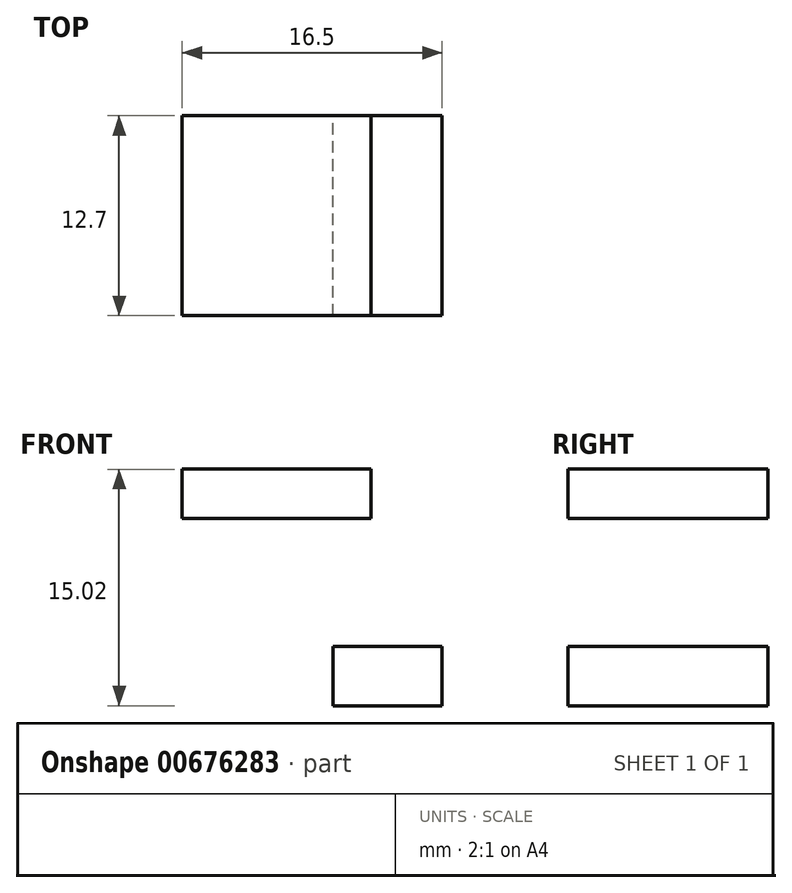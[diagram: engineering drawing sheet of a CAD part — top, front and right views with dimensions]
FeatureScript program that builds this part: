
annotation { "Feature Type Name" : "Feature", "Feature Type Description" : "" }
export const myFeature = defineFeature(function(context is Context, id is Id, definition is map)
    precondition{}
    {
        {
            var Q0;
            Q0=qCreatedBy(makeId("Front.planeOp"),FACE);
            var sketch = newSketch(context, id + "F0", { "sketchPlane" : qUnion([Q0])});
            skLineSegment(sketch, "E0.bottom", {"start": v(0, 0) * mm, "end": v(-6.91, 0) * mm});
            skLineSegment(sketch, "E0.top", {"start": v(0, 3.78) * mm, "end": v(-6.91, 3.78) * mm});
            skLineSegment(sketch, "E0.left", {"start": v(0, 0) * mm, "end": v(0, 3.78) * mm});
            skLineSegment(sketch, "E0.right", {"start": v(-6.91, 0) * mm, "end": v(-6.91, 3.78) * mm});
            skLineSegment(sketch, "E1.bottom", {"start": v(0, 3.78) * mm, "end": v(-4.52, 3.78) * mm});
            skLineSegment(sketch, "E1.top", {"start": v(0, 15.02) * mm, "end": v(-4.52, 15.02) * mm});
            skLineSegment(sketch, "E1.left", {"start": v(0, 3.78) * mm, "end": v(0, 15.02) * mm});
            skLineSegment(sketch, "E1.right", {"start": v(-4.52, 3.78) * mm, "end": v(-4.52, 15.02) * mm});
            skLineSegment(sketch, "E2.bottom", {"start": v(-4.52, 15.02) * mm, "end": v(-16.5, 15.02) * mm});
            skLineSegment(sketch, "E2.top", {"start": v(-4.52, 11.9) * mm, "end": v(-16.5, 11.9) * mm});
            skLineSegment(sketch, "E2.left", {"start": v(-4.52, 15.02) * mm, "end": v(-4.52, 11.9) * mm});
            skLineSegment(sketch, "E2.right", {"start": v(-16.5, 15.02) * mm, "end": v(-16.5, 11.9) * mm});
            skSolve(sketch);
        }
        {
            var Q0;
            Q0=makeQuery(id+"F0.imprint","IMPRINT",FACE,{"disambiguationData":[TD([[makeQuery(id+"F0.imprint","IMPRINT",EDGE,{"derivedFrom":sQuery(id+"F0.wireOp",EDGE,"E1.bottom")}),-1.0]])]});
            var Q1;
            Q1=makeQuery(id+"F0.imprint","IMPRINT",FACE,{"disambiguationData":[TD([[makeQuery(id+"F0.imprint","IMPRINT",EDGE,{"derivedFrom":sQuery(id+"F0.wireOp",EDGE,"E0.bottom")}),-1.0]])]});
            var Q2;
            Q2=makeQuery(id+"F0.imprint","IMPRINT",FACE,{"disambiguationData":[TD([[makeQuery(id+"F0.imprint","IMPRINT",EDGE,{"derivedFrom":sQuery(id+"F0.wireOp",EDGE,"E2.bottom")}),1.0]])]});
            extrude(context, id + "F1", {"entities" : qUnion([Q0, Q1, Q2]), "depth" : 12.7 * mm, "offsetDistance" : 25.4 * mm});
        }
    });
